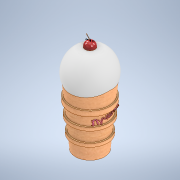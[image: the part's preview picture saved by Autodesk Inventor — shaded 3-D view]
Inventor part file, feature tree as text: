
AUTODESK INVENTOR PART (.ipt)
format: ipt  version: 2022 (Build 260153000, 153)  size: 505,344 bytes
history: native  units: mm
features: sketch x16, other x11, extrude x3, loft x2, revolve x2
ambient origin geometry x8: Origin, YZ Plane, XZ Plane, XY Plane, X Axis, Y Axis, Z Axis, Center Point
bodies: Body1 (feature_tree)
feature tree (34):
  other  "Твердое тело1"
  sketch  "Эскиз1"
  other  "РабПлоскость1"
  loft  "Лофт1"
  sketch  "Эскиз5"
  revolve  "Вращение1"
  other  "РабПлоскость7"
  sketch  "Эскиз7"
  sketch  "Эскиз8"
  sketch  "Эскиз9"
  extrude  "Выдавливание1"  Depth=50.0mm
  extrude  "Выдавливание2"  Depth=35.0mm
  other  "РабПлоскость8"
  sketch  "Эскиз12"
  revolve  "Вращение2"
  sketch  "Эскиз14"
  other  "РабПлоскость9"
  sketch  "Эскиз17"
  extrude  "Выдавливание4"  TaperAngle=0.0deg  [1 undecoded]
  sketch  "Эскиз21"
  other  "РабПлоскость12"
  other  "РабПлоскость13"
  other  "Рельеф1"
  other  "РабПлоскость14"
  loft  "Лофт4"
  sketch  "Эскиз3"
  sketch  "Эскиз6"
  other  "РабПлоскость5"
  other  "РабПлоскость6"
  sketch  "Эскиз10"
  sketch  "Эскиз13"
  sketch  "Эскиз19"
  sketch  "Эскиз23"
  sketch  "Эскиз24"
note: 1 required parameter value undecoded (feature->parameter linkage not recoverable at this tier; creation-order binding heuristic only, values carry confidence <= 0.55)
